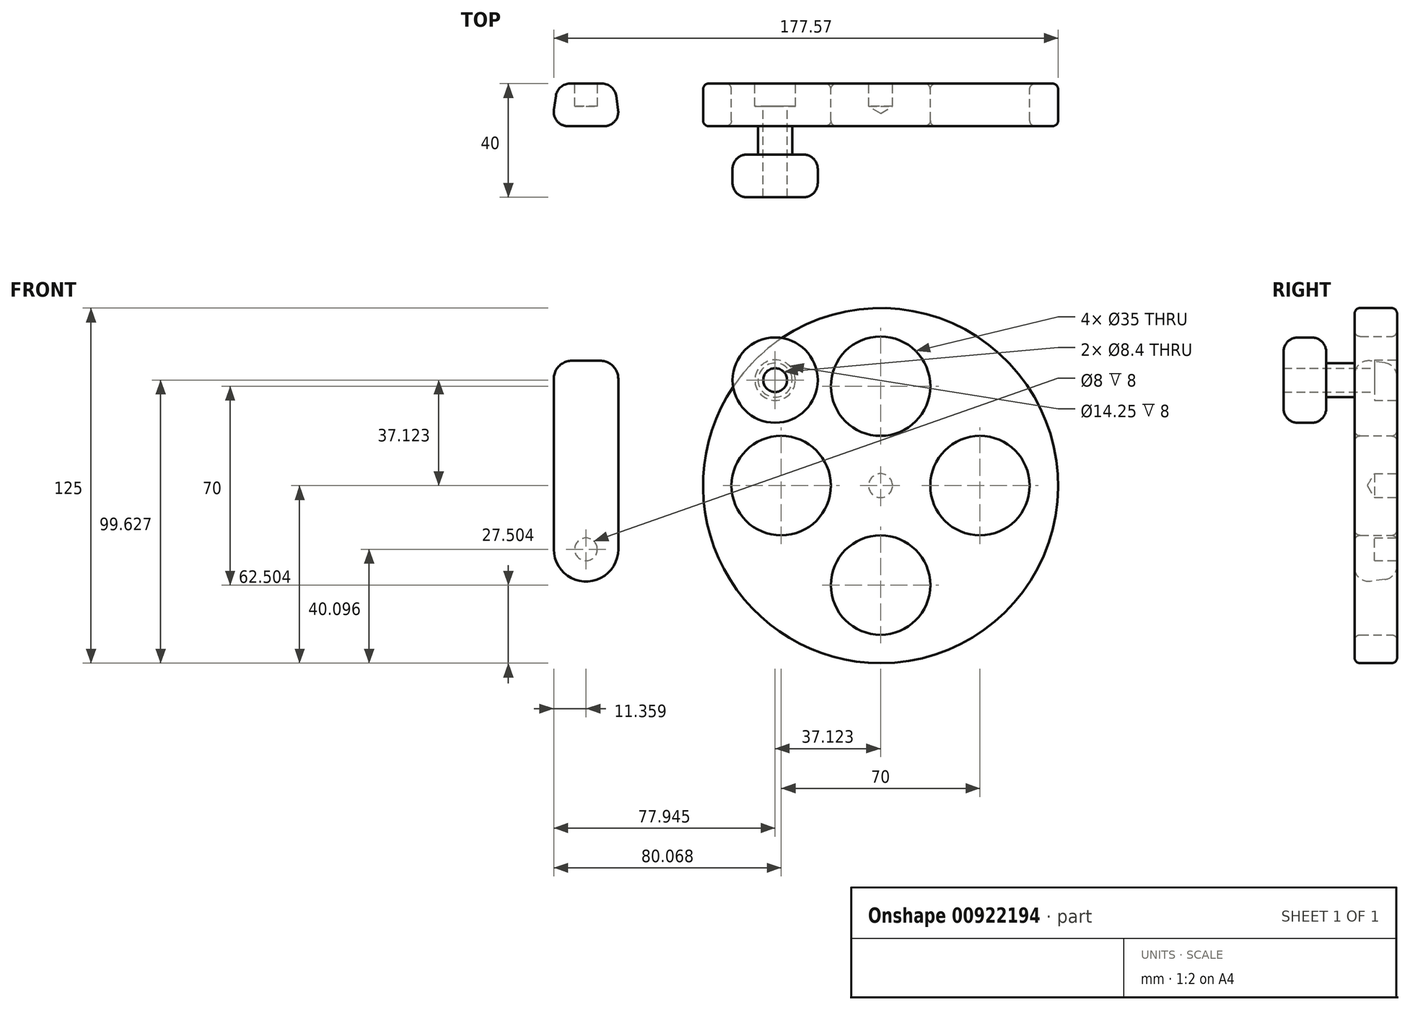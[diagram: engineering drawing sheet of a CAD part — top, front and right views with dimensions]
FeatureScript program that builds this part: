
annotation { "Feature Type Name" : "Feature", "Feature Type Description" : "" }
export const myFeature = defineFeature(function(context is Context, id is Id, definition is map)
    precondition{}
    {
        {
            var Q0;
            Q0=qCreatedBy(makeId("Front.planeOp"),FACE);
            var sketch = newSketch(context, id + "F0", { "sketchPlane" : qUnion([Q0])});
            skCircle(sketch, "E0", {"center": v(3.13, -1.55) * mm, "radius": 62.5 * mm});
            skLineSegment(sketch, "E1", {"start": v(3.13, -64.05) * mm, "end": v(3.13, 60.95) * mm, "construction": true});
            skLineSegment(sketch, "E2", {"start": v(-59.37, -1.55) * mm, "end": v(65.63, -1.55) * mm, "construction": true});
            skCircle(sketch, "E3", {"center": v(-31.87, -1.55) * mm, "radius": 17.5 * mm});
            skCircle(sketch, "E4", {"center": v(3.13, -1.55) * mm, "radius": 35 * mm, "construction": true});
            skCircle(sketch, "E5", {"center": v(3.13, 33.45) * mm, "radius": 17.5 * mm});
            skCircle(sketch, "E6", {"center": v(38.13, -1.55) * mm, "radius": 17.5 * mm});
            skCircle(sketch, "E7", {"center": v(3.13, -36.55) * mm, "radius": 17.5 * mm});
            skCircle(sketch, "E8", {"center": v(3.13, -1.55) * mm, "radius": 52.5 * mm, "construction": true});
            skLineSegment(sketch, "E9", {"start": v(3.13, -1.55) * mm, "end": v(-34, 35.58) * mm, "construction": true});
            skPoint(sketch, "E10", {"position": v(-34, 35.58) * mm});
            skSolve(sketch);
        }
        {
            var Q0;
            Q0=makeQuery(id+"F0.imprint","IMPRINT",FACE,{"disambiguationData":[TD([[makeQuery(id+"F0.imprint","IMPRINT",EDGE,{"derivedFrom":sQuery(id+"F0.wireOp",EDGE,"E0")}),1.0]])]});
            extrude(context, id + "F1", {"entities" : qUnion([Q0]), "depth" : 15 * mm, "offsetDistance" : 25 * mm});
        }
        {
            var Q0;
            Q0=makeQuery(id+"F1.opExtrude","CAP_EDGE",EDGE,{"disambiguationData":[OSD([sQuery(id+"F0.wireOp",EDGE,"E5")])],"isStart":false});
            var Q1;
            Q1=makeQuery(id+"F1.opExtrude","CAP_EDGE",EDGE,{"disambiguationData":[OSD([sQuery(id+"F0.wireOp",EDGE,"E5")])],"isStart":true});
            var Q2;
            Q2=makeQuery(id+"F1.opExtrude","CAP_EDGE",EDGE,{"disambiguationData":[OSD([sQuery(id+"F0.wireOp",EDGE,"E6")])],"isStart":false});
            var Q3;
            Q3=makeQuery(id+"F1.opExtrude","CAP_EDGE",EDGE,{"disambiguationData":[OSD([sQuery(id+"F0.wireOp",EDGE,"E6")])],"isStart":true});
            var Q4;
            Q4=makeQuery(id+"F1.opExtrude","CAP_EDGE",EDGE,{"disambiguationData":[OSD([sQuery(id+"F0.wireOp",EDGE,"E7")])],"isStart":false});
            var Q5;
            Q5=makeQuery(id+"F1.opExtrude","CAP_EDGE",EDGE,{"disambiguationData":[OSD([sQuery(id+"F0.wireOp",EDGE,"E7")])],"isStart":true});
            var Q6;
            Q6=makeQuery(id+"F1.opExtrude","CAP_FACE",FACE,{"disambiguationData":[OSD([sQuery(id+"F0.wireOp",EDGE,"E0"),sQuery(id+"F0.wireOp",EDGE,"E3"),sQuery(id+"F0.wireOp",EDGE,"E5"),sQuery(id+"F0.wireOp",EDGE,"E6"),sQuery(id+"F0.wireOp",EDGE,"E7")])],"isStart":false});
            var Q7;
            Q7=makeQuery(id+"F1.opExtrude","CAP_EDGE",EDGE,{"disambiguationData":[OSD([sQuery(id+"F0.wireOp",EDGE,"E3")])],"isStart":true});
            var Q8;
            Q8=makeQuery(id+"F1.opExtrude","CAP_EDGE",EDGE,{"disambiguationData":[OSD([sQuery(id+"F0.wireOp",EDGE,"E0")])],"isStart":true});
            fillet(context, id + "F2", {"entities" : qUnion([Q0, Q1, Q2, Q3, Q4, Q5, Q6, Q7, Q8]), "radius" : 2 * mm, "tangentPropagation" : true, "allowEdgeOverflow" : false});
        }
        {
            var Q0;
            Q0=sQuery(id+"F0.wireOp",VERTEX,"E10");
            var Q1;
            Q1=makeQuery(id+"F1.opExtrude","SWEPT_BODY",BODY,{"disambiguationData":[OSD([sQuery(id+"F0.wireOp",EDGE,"E0"),sQuery(id+"F0.wireOp",EDGE,"E3"),sQuery(id+"F0.wireOp",EDGE,"E5"),sQuery(id+"F0.wireOp",EDGE,"E6"),sQuery(id+"F0.wireOp",EDGE,"E7")])]});
            hole(context, id + "F3", {"style" : HoleStyle.C_BORE, "endStyle" : HoleEndStyle.THROUGH, "oppositeDirection" : true, "standardTappedOrClearance" : lookupTablePath({ "fit" : "Close", "standard" : "ISO", "size" : "M8", "type" : "Clearance" }), "standardBlindInLast" : lookupTablePath({ "fit" : "Close", "standard" : "ISO", "engagement" : "75%", "pitch" : "1.25 mm", "size" : "M8", "type" : "Clearance & tapped" }), "holeDiameter" : 8.4 * mm, "cBoreDiameter" : 14.25 * mm, "cBoreDepth" : 8 * mm, "majorDiameter" : 8 * mm, "isTappedThrough" : true, "tappedDepth" : 12 * mm, "tapClearance" : 3, "startFromSketch" : true, "locations" : qUnion([Q0]), "scope" : qUnion([Q1])});
        }
        {
            var Q0;
            Q0=sQuery(id+"F0.wireOp",VERTEX,"E0.center");
            var Q1;
            Q1=makeQuery(id+"F1.opExtrude","SWEPT_BODY",BODY,{"disambiguationData":[OSD([sQuery(id+"F0.wireOp",EDGE,"E0"),sQuery(id+"F0.wireOp",EDGE,"E3"),sQuery(id+"F0.wireOp",EDGE,"E5"),sQuery(id+"F0.wireOp",EDGE,"E6"),sQuery(id+"F0.wireOp",EDGE,"E7")])]});
            hole(context, id + "F4", {"style" : HoleStyle.SIMPLE, "endStyle" : HoleEndStyle.BLIND, "oppositeDirection" : true, "holeDiameter" : 8.4 * mm, "majorDiameter" : 5 * mm, "holeDepth" : 8 * mm, "isTappedThrough" : true, "tappedDepth" : 12 * mm, "tapClearance" : 3, "startFromSketch" : true, "locations" : qUnion([Q0]), "scope" : qUnion([Q1])});
        }
        {
            var Q0;
            Q0=makeQuery(id+"F1.opExtrude","CAP_FACE",FACE,{"disambiguationData":[OSD([sQuery(id+"F0.wireOp",EDGE,"E0"),sQuery(id+"F0.wireOp",EDGE,"E3"),sQuery(id+"F0.wireOp",EDGE,"E5"),sQuery(id+"F0.wireOp",EDGE,"E6"),sQuery(id+"F0.wireOp",EDGE,"E7")])],"isStart":false});
            var sketch = newSketch(context, id + "F5", { "sketchPlane" : qUnion([Q0])});
            skCircle(sketch, "E11", {"center": v(-34, 35.58) * mm, "radius": 15 * mm});
            skCircle(sketch, "E12", {"center": v(-34, 35.58) * mm, "radius": 6 * mm});
            skSolve(sketch);
        }
        {
            var Q0;
            Q0=makeQuery(id+"F5.imprint","IMPRINT",FACE,{"disambiguationData":[TD([[makeQuery(id+"F5.imprint","IMPRINT",EDGE,{"derivedFrom":sQuery(id+"F5.wireOp",EDGE,"E12")}),1.0]])]});
            var Q1;
            Q1=makeQuery(id+"F5.imprint","IMPRINT",FACE,{"disambiguationData":[TD([[makeQuery(id+"F5.imprint","IMPRINT",EDGE,{"derivedFrom":makeQuery(id+"F3.hole-0.boolean.opBoolean","INTERSECT",EDGE,{"derivedFrom":[makeQuery(id+"F1.opExtrude","CAP_FACE",FACE,{"disambiguationData":[OSD([sQuery(id+"F0.wireOp",EDGE,"E0"),sQuery(id+"F0.wireOp",EDGE,"E3"),sQuery(id+"F0.wireOp",EDGE,"E5"),sQuery(id+"F0.wireOp",EDGE,"E6"),sQuery(id+"F0.wireOp",EDGE,"E7")])],"isStart":false}),makeQuery(id+"F3.hole-0.opRevolve","SWEPT_FACE",FACE,{"disambiguationData":[OSD([sQuery(id+"F3.hole-0.sketch.wireOp",EDGE,"core_line_2")])]})]})}),-1.0]])]});
            extrude(context, id + "F6", {"entities" : qUnion([Q0, Q1]), "operationType" : NewBodyOperationType.ADD, "depth" : 25 * mm, "offsetDistance" : 25 * mm});
        }
        {
            var Q0;
            {var subQ5=sQuery(id+"F5.wireOp",EDGE,"E12");Q0=makeQuery(id+"F5.imprint","IMPRINT",FACE,{"disambiguationData":[TD([[makeQuery(id+"F5.imprint","IMPRINT",EDGE,{"derivedFrom":subQ5}),-1.0]])]});}
            var Q1;
            {var subQ0=sQuery(id+"F5.wireOp",EDGE,"E11");var subQ1=sQuery(id+"F0.wireOp",EDGE,"E0");var subQ2=makeQuery(id+"F2.opFillet","BLEND_EDGE",EDGE,{"blendedFrom":[makeQuery(id+"F1.opExtrude","CAP_EDGE",EDGE,{"disambiguationData":[OSD([subQ1])],"isStart":false}),makeQuery(id+"F1.opExtrude","CAP_FACE",FACE,{"disambiguationData":[OSD([subQ1,sQuery(id+"F0.wireOp",EDGE,"E3"),sQuery(id+"F0.wireOp",EDGE,"E5"),sQuery(id+"F0.wireOp",EDGE,"E6"),sQuery(id+"F0.wireOp",EDGE,"E7")])],"isStart":false})],"blendedInto":[makeQuery(id+"F1.opExtrude","CAP_FACE",FACE,{"disambiguationData":[OSD([subQ1,sQuery(id+"F0.wireOp",EDGE,"E3"),sQuery(id+"F0.wireOp",EDGE,"E5"),sQuery(id+"F0.wireOp",EDGE,"E6"),sQuery(id+"F0.wireOp",EDGE,"E7")])],"isStart":false})]});var subQ3=makeQuery(id+"F5.imprint","INTERSECT",VERTEX,{"disambiguationData":[OD(0.0)],"derivedFrom":[subQ2,subQ0]});Q1=makeQuery(id+"F5.imprint","IMPRINT",FACE,{"disambiguationData":[TD([[makeQuery(id+"F5.imprint","IMPRINT",EDGE,{"disambiguationData":[TD([[subQ3,1.0]])],"derivedFrom":subQ0}),1.0]])]});}
            extrude(context, id + "F7", {"entities" : qUnion([Q0, Q1]), "operationType" : NewBodyOperationType.ADD, "depth" : 25 * mm, "offsetDistance" : 25 * mm, "hasSecondDirection" : true, "secondDirectionOppositeDirection" : false, "secondDirectionDepth" : 10 * mm});
        }
        {
            var Q0;
            Q0=makeQuery(id+"F7.opExtrude","CAP_EDGE",EDGE,{"disambiguationData":[OSD([sQuery(id+"F5.wireOp",EDGE,"E11")])],"isStart":true});
            var Q1;
            Q1=makeQuery(id+"F7.opExtrude","CAP_EDGE",EDGE,{"disambiguationData":[OSD([sQuery(id+"F5.wireOp",EDGE,"E11")])],"isStart":false});
            fillet(context, id + "F8", {"entities" : qUnion([Q0, Q1]), "radius" : 5 * mm, "tangentPropagation" : true, "allowEdgeOverflow" : false});
        }
        {
            var Q0;
            Q0=qCreatedBy(makeId("Front.planeOp"),FACE);
            var sketch = newSketch(context, id + "F9", { "sketchPlane" : qUnion([Q0])});
            skLineSegment(sketch, "E13.bottom", {"start": v(-100.58, -33.95) * mm, "end": v(-100.58, -33.95) * mm});
            skLineSegment(sketch, "E13.top", {"start": v(-105.58, 41.05) * mm, "end": v(-95.58, 41.05) * mm});
            skLineSegment(sketch, "E13.left", {"start": v(-110.58, -23.95) * mm, "end": v(-110.58, 36.05) * mm});
            skLineSegment(sketch, "E13.right", {"start": v(-90.58, -23.95) * mm, "end": v(-90.58, 36.05) * mm});
            skPoint(sketch, "E14.visualSharp", {"position": v(-110.58, 41.05) * mm});
            skArc(sketch, "E14.filletArc", {"start": v(-105.58, 41.05) * mm, "mid": v(-109.12, 39.58) * mm, "end": v(-110.58, 36.05) * mm});
            skPoint(sketch, "E15.visualSharp", {"position": v(-90.58, 41.05) * mm});
            skArc(sketch, "E15.filletArc", {"start": v(-90.58, 36.05) * mm, "mid": v(-92.05, 39.58) * mm, "end": v(-95.58, 41.05) * mm});
            skPoint(sketch, "E16.visualSharp", {"position": v(-90.58, -33.95) * mm});
            skPoint(sketch, "E17.visualSharp", {"position": v(-110.58, -33.95) * mm});
            skArc(sketch, "E18", {"start": v(-110.58, -23.95) * mm, "mid": v(-100.58, -33.95) * mm, "end": v(-90.58, -23.95) * mm});
            skCircle(sketch, "E19", {"center": v(-100.58, -23.95) * mm, "radius": 4 * mm});
            skSolve(sketch);
        }
        {
            var Q0;
            Q0=makeQuery(id+"F9.imprint","IMPRINT",FACE,{"disambiguationData":[TD([[makeQuery(id+"F9.imprint","IMPRINT",EDGE,{"derivedFrom":sQuery(id+"F9.wireOp",EDGE,"E13.top")}),-1.0]])]});
            var Q1;
            Q1=makeQuery(id+"F9.imprint","IMPRINT",FACE,{"disambiguationData":[TD([[makeQuery(id+"F9.imprint","IMPRINT",EDGE,{"derivedFrom":sQuery(id+"F9.wireOp",EDGE,"E19")}),1.0]])]});
            extrude(context, id + "F10", {"entities" : qUnion([Q0, Q1]), "depth" : 15 * mm, "offsetDistance" : 25 * mm, "hasDraft" : true, "draftAngle" : 8 * degree});
        }
        {
            var Q0;
            Q0=makeQuery(id+"F10.opExtrude","CAP_EDGE",EDGE,{"disambiguationData":[OSD([sQuery(id+"F9.wireOp",EDGE,"E13.left")])],"isStart":true});
            var Q1;
            Q1=makeQuery(id+"F10.opExtrude","CAP_EDGE",EDGE,{"disambiguationData":[OSD([sQuery(id+"F9.wireOp",EDGE,"E18")])],"isStart":true});
            var Q2;
            Q2=makeQuery(id+"F10.opExtrude","CAP_EDGE",EDGE,{"disambiguationData":[OSD([sQuery(id+"F9.wireOp",EDGE,"E13.left")])],"isStart":false});
            fillet(context, id + "F11", {"entities" : qUnion([Q0, Q1, Q2]), "radius" : 5 * mm, "tangentPropagation" : true, "allowEdgeOverflow" : false});
        }
        {
            var Q0;
            Q0=makeQuery(id+"F9.imprint","IMPRINT",FACE,{"disambiguationData":[TD([[makeQuery(id+"F9.imprint","IMPRINT",EDGE,{"derivedFrom":sQuery(id+"F9.wireOp",EDGE,"E19")}),1.0]])]});
            var Q1;
            Q1=sQuery(id+"F9.wireOp",EDGE,"UjE05TkB-bLy2-uCZd-BnVA-CTvrlyNxcXJ8");
            extrude(context, id + "F12", {"entities" : qUnion([Q0]), "operationType" : NewBodyOperationType.REMOVE, "surfaceEntities" : qUnion([Q1]), "depth" : 8 * mm, "offsetDistance" : 25 * mm});
        }
    });
